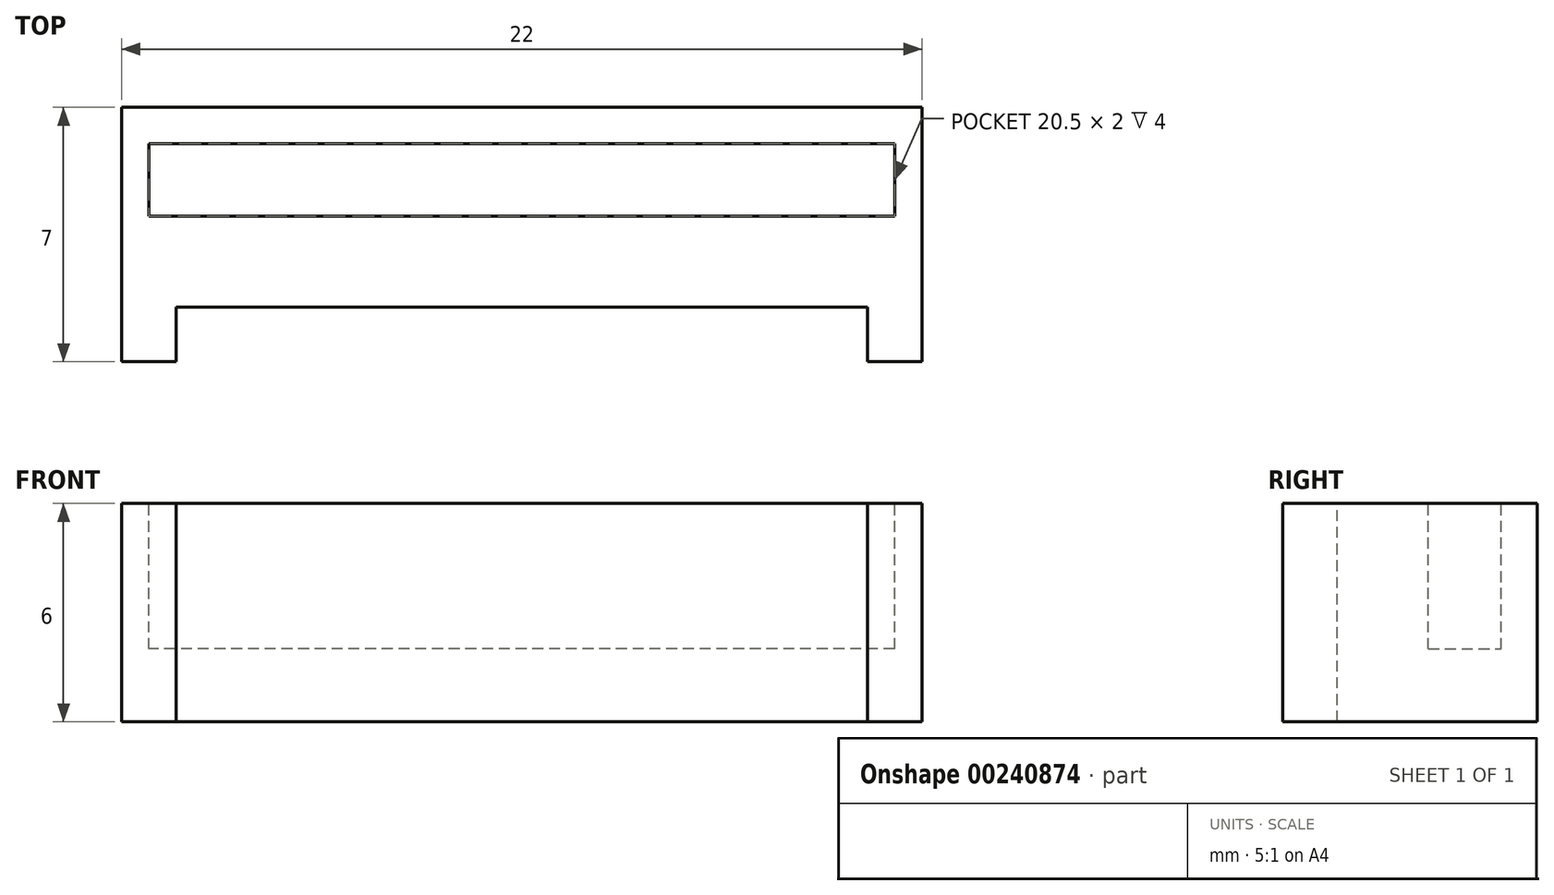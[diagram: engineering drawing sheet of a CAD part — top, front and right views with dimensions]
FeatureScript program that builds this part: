
annotation { "Feature Type Name" : "Feature", "Feature Type Description" : "" }
export const myFeature = defineFeature(function(context is Context, id is Id, definition is map)
    precondition{}
    {
        {
            var Q0;
            Q0=qCreatedBy(makeId("Top.planeOp"),FACE);
            var sketch = newSketch(context, id + "F0", { "sketchPlane" : qUnion([Q0])});
            skLineSegment(sketch, "E0.bottom", {"start": v(11, -3.5) * mm, "end": v(-11, -3.5) * mm});
            skLineSegment(sketch, "E0.top", {"start": v(11, 3.5) * mm, "end": v(-11, 3.5) * mm});
            skLineSegment(sketch, "E0.left", {"start": v(11, -3.5) * mm, "end": v(11, 3.5) * mm});
            skLineSegment(sketch, "E0.right", {"start": v(-11, -3.5) * mm, "end": v(-11, 3.5) * mm});
            skPoint(sketch, "E0.middle", {"position": v(0, 0) * mm});
            skSolve(sketch);
        }
        {
            var Q0;
            Q0 = qSketchRegion(id + "F0", true);
            extrude(context, id + "F1", {"entities" : qUnion([Q0]), "depth" : 6 * mm});
        }
        {
            var Q0;
            Q0=makeQuery(id+"F1.opExtrude","CAP_FACE",FACE,{"disambiguationData":[OSD([sQuery(id+"F0.wireOp",EDGE,"E0.bottom"),sQuery(id+"F0.wireOp",EDGE,"E0.top"),sQuery(id+"F0.wireOp",EDGE,"E0.left"),sQuery(id+"F0.wireOp",EDGE,"E0.right")])],"isStart":false});
            var sketch = newSketch(context, id + "F2", { "sketchPlane" : qUnion([Q0])});
            skLineSegment(sketch, "E1.bottom", {"start": v(10.25, 0.5) * mm, "end": v(-10.25, 0.5) * mm});
            skLineSegment(sketch, "E1.top", {"start": v(10.25, 2.5) * mm, "end": v(-10.25, 2.5) * mm});
            skLineSegment(sketch, "E1.left", {"start": v(10.25, 0.5) * mm, "end": v(10.25, 2.5) * mm});
            skLineSegment(sketch, "E1.right", {"start": v(-10.25, 0.5) * mm, "end": v(-10.25, 2.5) * mm});
            skPoint(sketch, "E1.middle", {"position": v(0, 1.5) * mm});
            skLineSegment(sketch, "E2", {"start": v(0, 3.5) * mm, "end": v(0, 2.5) * mm, "construction": true});
            skSolve(sketch);
        }
        {
            var Q0;
            Q0 = qSketchRegion(id + "F2", true);
            extrude(context, id + "F3", {"entities" : qUnion([Q0]), "operationType" : NewBodyOperationType.REMOVE, "oppositeDirection" : true, "depth" : 4 * mm});
        }
        {
            var Q0;
            Q0=makeQuery(id+"F1.opExtrude","SWEPT_FACE",FACE,{"disambiguationData":[OSD([sQuery(id+"F0.wireOp",EDGE,"E0.bottom")])]});
            var sketch = newSketch(context, id + "F4", { "sketchPlane" : qUnion([Q0])});
            skLineSegment(sketch, "E3.bottom", {"start": v(9.5, 0) * mm, "end": v(-9.5, 0) * mm});
            skLineSegment(sketch, "E3.top", {"start": v(9.5, 6) * mm, "end": v(-9.5, 6) * mm});
            skLineSegment(sketch, "E3.left", {"start": v(9.5, 0) * mm, "end": v(9.5, 6) * mm});
            skLineSegment(sketch, "E3.right", {"start": v(-9.5, 0) * mm, "end": v(-9.5, 6) * mm});
            skPoint(sketch, "E3.middle", {"position": v(0, 3) * mm});
            skSolve(sketch);
        }
        {
            var Q0;
            Q0 = qSketchRegion(id + "F4", true);
            extrude(context, id + "F5", {"entities" : qUnion([Q0]), "operationType" : NewBodyOperationType.REMOVE, "oppositeDirection" : true, "depth" : 1.5 * mm});
        }
    });
